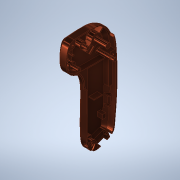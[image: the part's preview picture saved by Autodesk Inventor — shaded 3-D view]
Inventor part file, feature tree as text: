
AUTODESK INVENTOR PART (.ipt)
format: ipt  version: 2020.1 (Build 241239000, 239)  size: 1,648,128 bytes
history: native  units: mm
features: extrude x20, reference x20, sketch x16, other x15, plane x8, fillet x4, chamfer x3, projected_geometry x2, shell x1, draft x1, mirror x1, emboss x1, loft x1, revolve x1
ambient origin geometry x8: Origin, YZ Plane, XZ Plane, XY Plane, X Axis, Y Axis, Z Axis, Center Point
bodies: Body1 (feature_tree), Body2 (feature_tree)
feature tree (94):
  other  "Remote Bottom Shell"
  other  "Outline"
  other  "Acceleration Knob"
  extrude  "Extrusion1"  Depth=33.5mm
  chamfer  "Chamfer1"  Distance=200.0mm Angle=360.0deg
  shell  "Shell1"  Thickness=12.0mm
  extrude  "Extrusion2"  Depth=1.5mm
  sketch  "Sketch8"  dims[d0=131.0mm d86=33.5mm]
  extrude  "Extrusion5"  Depth=4.2mm TaperAngle=0.0deg
  extrude  "Extrusion6"  Depth=12.0mm
  plane  "Work Plane3"
  extrude  "Extrusion7"  Depth=5.0mm
  sketch  "Sketch10"  dims[d96=4.6mm d97=2.0mm d98=45.0deg d99=1.5mm]
  extrude  "Extrusion8"  Depth=6.5mm
  extrude  "Extrusion9"  Depth=4.0mm
  plane  "Work Plane4"
  sketch  "Sketch11"  dims[d103=0.35mm d104=4.2mm d105=0.0mm]
  extrude  "Extrusion10"  Depth=1.5mm
  extrude  "Extrusion11"  Depth=1.5mm
  plane  "Work Plane5"
  extrude  "Extrusion12"  Depth=2.5mm
  extrude  "Extrusion13"  Depth=4.0mm
  extrude  "Extrusion14"  Depth=4.0mm
  extrude  "Extrusion15"  Depth=1.5mm
  chamfer  "Chamfer3"  Angle=45.0deg  [1 undecoded]
  plane  "Work Plane6"
  extrude  "Extrusion16"  Depth=2.0mm
  draft  "FaceDraft1"
  extrude  "Extrusion17"  Depth=4.0mm
  fillet  "Fillet1"  Radius=1.0mm
  sketch  "Sketch17"  dims[d129=8.0mm d130=1.5mm]
  plane  "Work Plane7"
  extrude  "Extrusion18"  Depth=1.0mm
  plane  "Work Plane8"
  mirror  "Mirror1"
  extrude  "Extrusion20"  Depth=4.5mm
  emboss  "Emboss1"
  plane  "Work Plane9"
  extrude  "Extrusion21"  TaperAngle=45.0deg  [1 undecoded]
  extrude  "Extrusion22"  Depth=1.5mm
  chamfer  "Chamfer4"  Distance=1.5mm
  loft  "Loft1"
  fillet  "Fillet2"  Radius=82.0mm
  fillet  "Fillet3"  Radius=4.623mm
  plane  "Work Plane10"
  revolve  "Revolution1"  [1 undecoded]
  fillet  "Fillet4"  Radius=20.2mm
  extrude  "Extrusion23"  Depth=4.0mm TaperAngle=0.0deg
  other  "Image1"
  sketch  "Sketch9"  dims[d87=31.0mm d88=200.0mm d90=360.0deg d94=12.0mm d95=0.0mm]
  sketch  "Sketch12"  dims[d121=6.0mm d122=12.0mm]
  sketch  "Sketch14"  dims[d123=8.0mm d124=5.0mm]
  sketch  "Sketch15"  dims[d125=7.5mm d126=6.5mm]
  sketch  "Sketch16"  dims[d127=45.0deg d128=4.0mm]
  reference  "Reference2"
  reference  "Reference3"
  reference  "Reference4"
  other  "Plate"
  other  "Plate Solid"
  sketch  "Sketch19"  dims[d131=1.5mm d134=1.5mm]
  sketch  "Sketch20"  dims[d135=3.5mm d136=2.5mm]
  reference  "Reference5"
  reference  "Reference6"
  reference  "Reference7"
  reference  "Reference8"
  reference  "Reference9"
  reference  "Reference10"
  reference  "Reference11"
  reference  "Reference12"
  reference  "Reference13"
  reference  "Reference14"
  reference  "Reference15"
  reference  "Reference16"
  sketch  "Sketch21"  dims[d137=1.0mm d138=4.0mm]
  sketch  "Sketch22"  dims[d140=45.0deg d141=4.0mm]
  sketch  "Sketch23"  dims[d142=8.5mm d143=1.5mm]
  projected_geometry  "Projected Loop1"
  other  "Work Axis1"
  sketch  "Sketch24"  dims[d144=1.0mm]
  projected_geometry  "Projected Loop2"
  sketch  "Sketch25"  dims[d145=2.0mm d146=45.0deg d147=2.0mm d148=4.0mm d150=1.0mm d151=1.0mm d152=4.5mm d153=45.0deg d156=1.5mm d157=1.5mm d159=25.0mm d160=82.0mm d161=4.623mm d163=4.0mm d164=20.2mm d165=0.0mm d166=4.0mm d167=0.0mm d168=20.7mm d169=4.0mm d170=0.0mm d171=4.0mm d172=0.0mm d173=1.0mm d174=0.0mm d175=-3.0mm d176=1.0mm d177=0.0mm d178=9.2mm d179=0.0mm d180=8.5mm d181=9.2mm d182=0.0mm d197=5.5mm d198=0.0mm d199=4.5mm d200=0.0mm d201=26.0mm d202=36.0mm d204=26.0mm d205=20.0mm d206=1.0mm d208=10.0mm d209=4.5mm d210=8.0mm d211=18.2mm d212=14.2mm d213=4.5mm d214=5.0mm d215=1.2mm d216=4.0mm d217=4.0mm d218=2.1mm d220=5.2mm d221=5.2mm d224=7.4mm d225=0.0mm d226=1.0mm d227=2.0mm d228=45.0deg d229=0.001mm d230=10.0mm d231=0.0mm d232=45.0deg d234=3.0mm d235=0.0mm d236=1.0mm d237=13.4mm d238=1.2mm d239=2.75mm d240=2.5mm d241=2.5mm d242=1.9mm d243=0.5mm d244=0.0mm d246=1.0mm d247=3.5mm d248=2.0mm d251=0.8mm d252=0.0mm d254=0.5mm d255=0.0mm d257=7.65mm d258=1.85mm d259=1.85mm d260=1.020476mm d261=1.020476mm d264=7.65mm d265=0.0mm d266=6.0mm d267=0.0mm d268=0.2mm d269=2.0mm d270=45.0deg d271=2.0mm d272=1.5mm d273=1.0mm d274=1.5mm d275=10.0mm d276=90.0deg d277=10.0mm d278=90.0deg d279=8.0mm d280=8.0mm d281=0.0mm d282=1.5mm d283=90.0deg d284=0.5mm d289=3.0mm d290=0.523599mm]
  reference  "Reference17"
  reference  "Reference18"
  reference  "Reference19"
  reference  "Reference20"
  reference  "Reference21"
  parser-record x1  (decoder bookkeeping rows leaked as tree rows — omitted from the tree; the rows remain in map.json)
  other  "Remote.iam"
  other  "Remote Top Shell:1"
  other  "SPDT Mini Slide Switch:1"
  other  "switch body 2_5431"
  other  "Microswitch Subminiature Lever SPDT Through Hole:1"
  other  "Lipo Charger - TP4056:1"
  other  "bOARD"
note: 3 required parameter values undecoded (feature->parameter linkage not recoverable at this tier; creation-order binding heuristic only, values carry confidence <= 0.55)
note: 1 file-system path scrubbed to <path> (originals preserved in map.json)